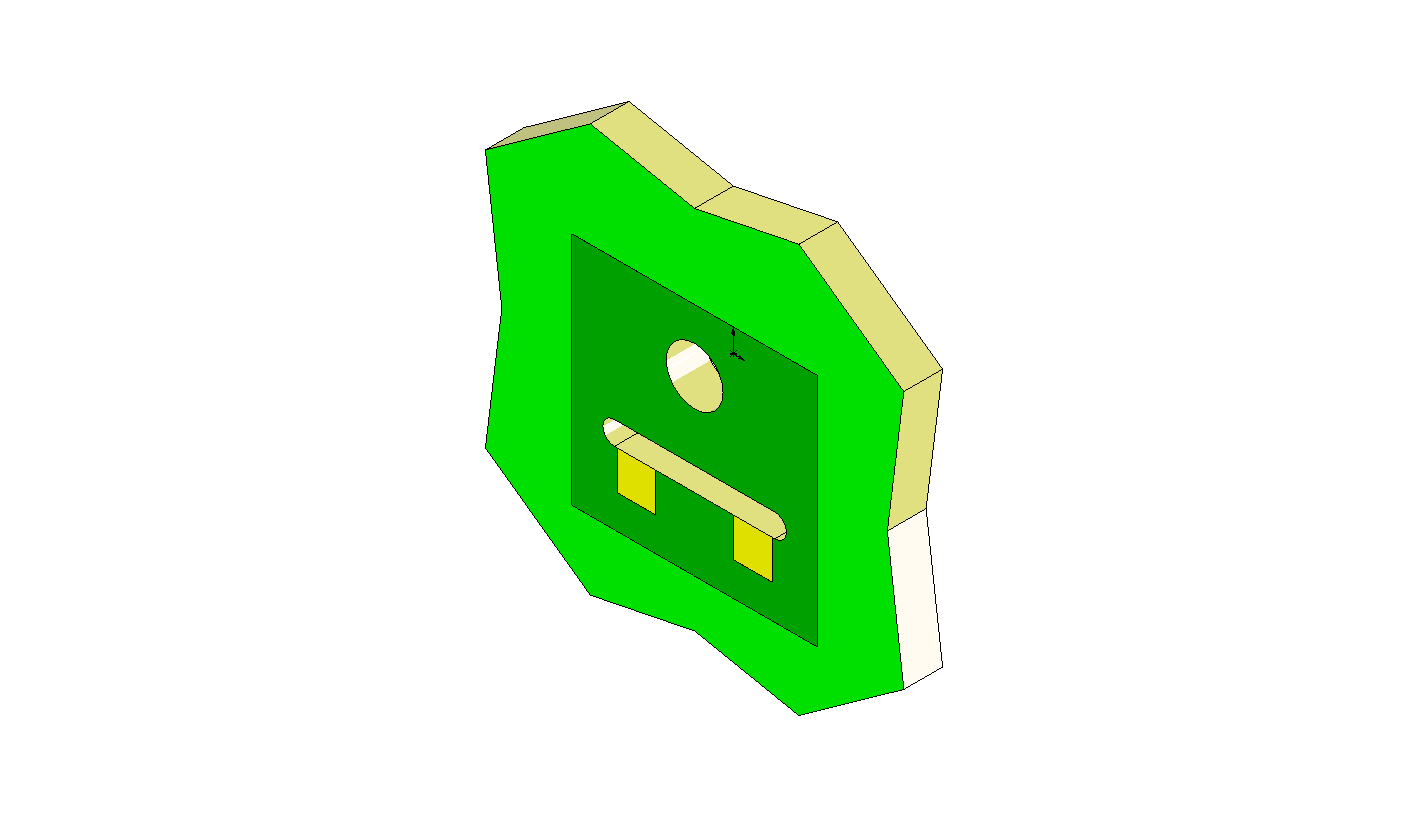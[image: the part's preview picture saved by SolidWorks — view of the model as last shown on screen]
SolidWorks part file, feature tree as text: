
SOLIDWORKS PART (.sldprt)
format: sldprt  version: not decoded by parser v0  size: 249,344 bytes
history: native  units: mm
features: sketch x4, extrude x3, material x1, cut_extrude x1 (+11 scaffold rows collapsed)
feature tree (20):
  scaffold x11  (default folders/planes/origin — collapsed)
  material  "Material <not specified>"
  sketch  "Sketch1"  dims[c1.D1=2.2mm c1.D2=3.0mm c1.D3=0.9mm c1.D4=6.2mm c1.D5=0.9mm c2.D4=6.2mm c2.D5=4.0mm c2.D6=8.0mm c2.D7=2.0mm c2.D8=12.0mm c2.D9=2.0mm c2.D10=2.0mm c2.D11=2.0mm c2.D12=~0.464967mm]
  extrude  "Extrude1"  Depth=1.5mm
  sketch  "Sketch5"  dims[D1=9.5mm D2=2.4mm D3=6.7mm]
  cut_extrude  "Cut-Extrude2"  Depth=0.001mm
  sketch  "Sketch6"  dims[D3=4.0mm D1=1.5mm D2=1.5mm]
  extrude  "Extrude5"  Depth=0.001mm
  sketch  "Sketch7"  dims[D1=4.0mm D2=1.5mm D3=1.4mm D4=1.5mm]
  extrude  "Extrude6"  Depth=0.001mm
decode coverage: 8 of 8 modeling features carry decoded parameters
note: ~ marks probable driven/reference dimensions
note: suppression state not decoded; provenance and decode notes live in map.json
